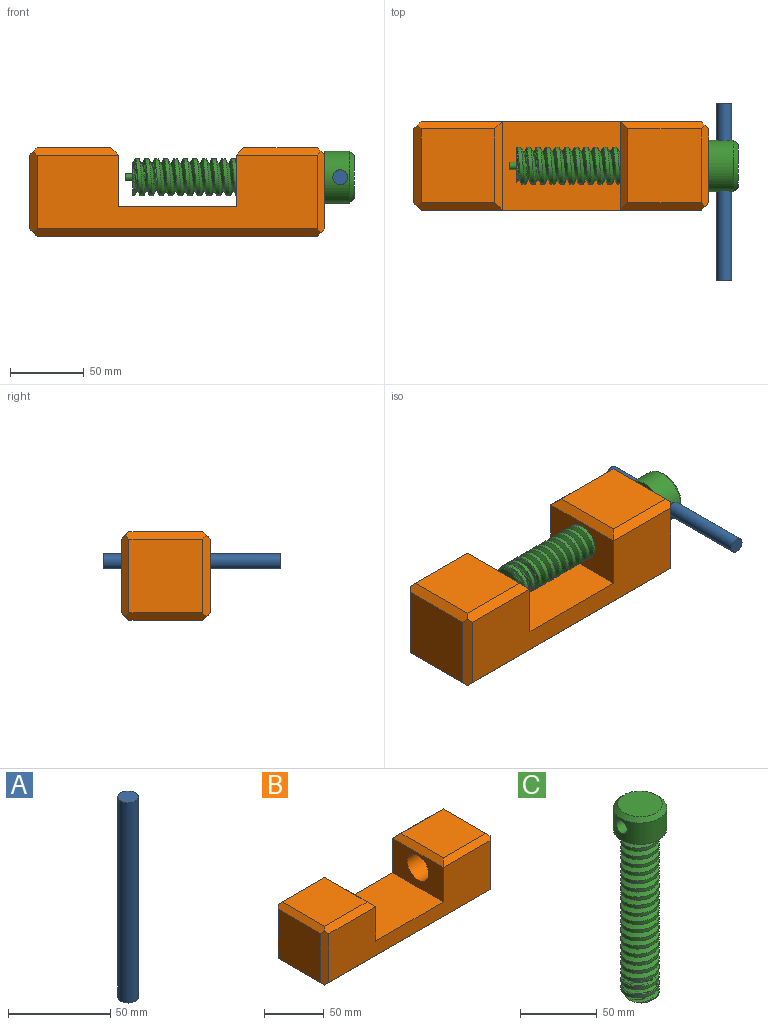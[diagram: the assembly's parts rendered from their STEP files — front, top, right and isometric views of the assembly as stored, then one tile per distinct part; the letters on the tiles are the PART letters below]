
ASSEMBLY  parts=3 mates=2
PART A: 3 faces, bbox 10x10x120 mm
  f0: cylinder r=5mm len=120mm, axis (0,0,-1), area 3769.9mm2, adj f1,f2
  f1: plane 10x10mm, normal (0,0,1), area 78.5mm2, adj f0
  f2: plane 10x10mm, normal (0,0,-1), area 78.5mm2, adj f0
PART B: 27 faces, bbox 200x60x60 mm
  f0: plane 50x50mm, normal (-1,0,0), area 2500mm2, adj f11,f12,f14,f20
  f1: plane 190x50mm, normal (0,0,-1), area 9500mm2, adj f13,f14,f15,f26
  f2: plane 50x50mm, normal (1,0,0), area 2009.1mm2, adj f10,f16,f24,f25,f26
  f3: plane 50x50mm, normal (0,0,1), area 2500mm2, adj f16,f17,f18,f19
  f4: plane 60x35mm, normal (-1,0,0), area 1609.1mm2, adj f5,f8,f9,f10,f19
  f5: plane 80x60mm, normal (0,0,1), area 4800mm2, adj f4,f6,f8,f9
  f6: plane 60x35mm, normal (1,0,0), area 2100mm2, adj f5,f8,f9,f22
  f7: plane 50x50mm, normal (0,0,1), area 2500mm2, adj f20,f21,f22,f23
  f8: plane 190x50mm, normal (0,-1,0), area 6700mm2, adj f4,f5,f6,f12,f13,f17,f21,f24
  f9: plane 190x50mm, normal (0,1,0), area 6700mm2, adj f4,f5,f6,f11,f15,f18,f23,f25
  f10: cylinder r=12.5mm len=60mm, axis (1,0,0), area 4712.4mm2, adj f2,f4
  f11: plane 55x5mm, normal (-0.71,0.71,0), area 371.2mm2, adj f0,f9,f14,f15,f20,f23
  f12: plane 55x5mm, normal (-0.71,-0.71,0), area 371.2mm2, adj f0,f8,f13,f14,f20,f21
  f13: plane 195x5mm, normal (0,-0.71,-0.71), area 1361.2mm2, adj f1,f8,f12,f14,f24,f26
  f14: plane 55x5mm, normal (-0.71,0,-0.71), area 371.2mm2, adj f0,f1,f11,f12,f13,f15
  f15: plane 195x5mm, normal (0,0.71,-0.71), area 1361.2mm2, adj f1,f9,f11,f14,f25,f26
  f16: plane 55x5mm, normal (0.71,0,0.71), area 371.2mm2, adj f2,f3,f17,f18,f24,f25
  f17: plane 57.5x5mm, normal (0,-0.71,0.71), area 380.1mm2, adj f3,f8,f16,f19,f24
  f18: plane 57.5x5mm, normal (0,0.71,0.71), area 380.1mm2, adj f3,f9,f16,f19,f25
  f19: plane 60x5mm, normal (-0.71,0,0.71), area 388.9mm2, adj f3,f4,f17,f18
  f20: plane 55x5mm, normal (-0.71,0,0.71), area 371.2mm2, adj f0,f7,f11,f12,f21,f23
  f21: plane 57.5x5mm, normal (0,-0.71,0.71), area 380.1mm2, adj f7,f8,f12,f20,f22
  f22: plane 60x5mm, normal (0.71,0,0.71), area 388.9mm2, adj f6,f7,f21,f23
  f23: plane 57.5x5mm, normal (0,0.71,0.71), area 380.1mm2, adj f7,f9,f11,f20,f22
  f24: plane 55x5mm, normal (0.71,-0.71,0), area 371.2mm2, adj f2,f8,f13,f16,f17,f26
  f25: plane 55x5mm, normal (0.71,0.71,0), area 371.2mm2, adj f2,f9,f15,f16,f18,f26
  f26: plane 55x5mm, normal (0.71,0,-0.71), area 371.2mm2, adj f1,f2,f13,f15,f24,f25
PART C: 12 faces, bbox 35x35x155 mm
  f0: cylinder r=12.5mm len=130mm, axis (0,0,-1), area 5546.3mm2, adj f1,f4,f7,f8,f9
  f1: plane 23.83x22.36mm, normal (0,0,-1), area 395.2mm2, adj f0,f7,f8,f10
  f2: cylinder r=17.5mm len=35mm, axis (0,0,-1), area 1710.5mm2, adj f4,f5,f6
  f3: plane 29x29mm, normal (0,0,1), area 660.5mm2, adj f6
  f4: plane 35x35mm, normal (0,0,-1), area 471.2mm2, adj f0,f2
  f5: cylinder r=5mm len=35mm, axis (1,0,0), area 1076.8mm2, adj f2
  f6: cone r=14.5mm half-angle=45deg, axis (0,0,-1), area 426.5mm2, adj f2,f3
  f7: bspline ~130.92x28.87mm, area 5259.7mm2, adj f0,f1,f8,f9
  f8: bspline ~132x28.87mm, area 5358.7mm2, adj f0,f1,f7,f9
  f9: plane 4x3.46mm, normal (0,-1,0), area 6.9mm2, adj f0,f7,f8
  f10: cylinder r=2.5mm len=5mm, axis (0,0,1), area 78.5mm2, adj f1,f11
  f11: plane 5x5mm, normal (0,0,-1), area 19.6mm2, adj f10
PLACE A rot(axis=(0,-0.71,0.71),180deg) t=(117.81,51.91,18.08)mm
PLACE B t=(-25.5,39.63,9.39)mm
PLACE C rot(axis=(0.58,0.58,0.58),120deg) t=(-22.65,9.63,18.08)mm
MATE slider A.f0 <-> C.f5  axis (0,1,0) through (117.81,-8.09,18.08)mm
MATE slider C.f0 <-> B.f10  axis (-1,0,0) through (107.35,9.63,18.08)mm
